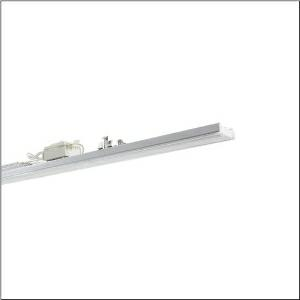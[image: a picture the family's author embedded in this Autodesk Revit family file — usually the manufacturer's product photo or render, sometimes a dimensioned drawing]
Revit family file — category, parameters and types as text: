
# Revit family: licross_21_recessed_mo_52tl127n485g
name_source: partatom
category: Lighting Fixtures
units: mm (PartAtom-declared; Revit-internal decimal feet)

## family parameters
Cut with Voids When Loaded = No
Host = Face
Light Source = No
Part Type = Normal
Room Calculation Point = No
Round Connector Dimension = Use Diameter
Shared = No

## types (1)
- Licross 21 Recessed MO (1 x LED, 8820 lm, 47.9 W, 4000K)
    Apparent Load = 48 VA
    CIE Flux Codes = 72 92 99 100 100
    Color Rendering = 80
    Color Temperature = 4000K
    Default Elevation = 1800 mm
    Description = Licross 21 Recessed MO, luminaire insert, of sheet steel, galvanised, coil coated, white, length: 1.500mm, width: 66mm, height: 67mm, LED rated luminous flux: 8.820lm, light colour: 840, SDCM (Standard Deviation of Colour Matching)MacAdam ≤ 3 SDCM (initial), control gear: ON/OFF, with plug, 3-pole, with phase selection, mains connection: 220..240V, AC, 50/60Hz, rated input power: 48W, internal wiring halogen-free, primary optical cover: cover, of PMMA, light emission: direct distribution, primary light characteristic: symmetric, protection rating (complete): IP40, insulation class (complete): insulation class I (protective earthing), certification: CE, ENEC, VDE, UKCA, protection symbol: D if used in an environment without relevant dust loads with corresponding accessories, impact resistance: IK06, permissible ambient temperature for indoor applications: -35..+40°C, corresponds to IFS (International Featured Standards) requirements for safety and quality in the food industry, reducing of maximum allowable ambient temperature of 5°C with ceiling mounting, LABS conformity tested according to VDMA 24364:2018-05, The light source and the operating device comply with the requirements of the Ecodesign Regulation (EU) 2019/2020 and are replaceable in accordance with this regulation, packaging unit: 1 piece
    Height = 58 mm
    Lamp = 1 x LED
    Lamp Light Flux = 8820 lm
    Lamp Power = 47.9 W
    Lamp count = 1
    Length = 1500 mm
    Luminous efficacy = 184 lm/W
    Manufacturer = Siteco
    ModVariant = No
    Model = 52TL127N485G
    Mounting Place = Ceiling
    Mounting Type = Pendant
    Number of Poles = 1
    OnlyDefault = Yes
    Power Factor = 1
    Product Name = Licross 21 Recessed MO
    Product group = luminaire insert | ceiling pendant
    ProductGroupID = 901
    Protection Class = Protection class I
    Protection Degree = IP 40
    RLX_Detail_Level = 1
    RLX_Emergency_Light_Flux = 0 lm
    RLX_Emergency_Type = 0
    RLX_Emergency_Type_DB = No
    RlxData = <blob elided: 21185 chars, md5=7b964a0b>
    Socket = socket
    Standby Power = 0 W
    System Light Flux = 8820 lm
    System Power = 48 W
    Type Comments = Product without accessories
    Type Image = l_1296930.jpg
    URL = http://relux.com
    VarID = ---
    Voltage = 0 V
    Weight = 0.00 kg
    Width = 66 mm

## geometry (parser evidence)
native form markers: Blend x4, Sweep x9
no freeform markers — native parametric forms only
